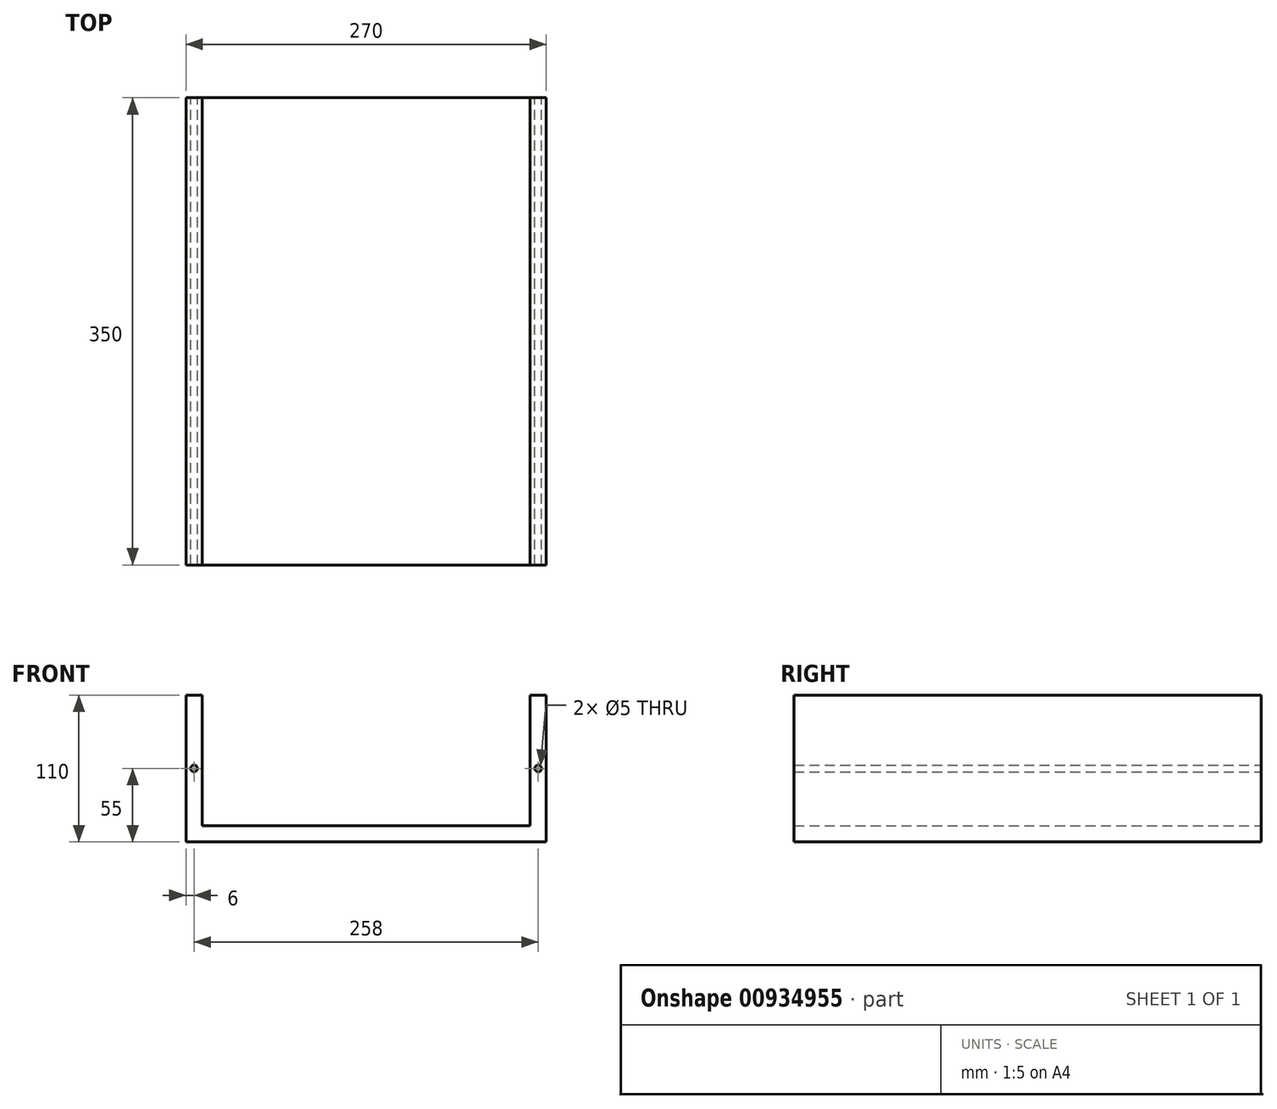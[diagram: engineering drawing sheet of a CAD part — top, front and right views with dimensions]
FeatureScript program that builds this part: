
annotation { "Feature Type Name" : "Feature", "Feature Type Description" : "" }
export const myFeature = defineFeature(function(context is Context, id is Id, definition is map)
    precondition{}
    {
        {
            var Q0;
            Q0=qCreatedBy(makeId("Front.planeOp"),FACE);
            var sketch = newSketch(context, id + "F0", { "sketchPlane" : qUnion([Q0])});
            skLineSegment(sketch, "E0", {"start": v(0, 0) * mm, "end": v(270, 0) * mm});
            skLineSegment(sketch, "E1", {"start": v(0, 0) * mm, "end": v(0, 110) * mm});
            skLineSegment(sketch, "E2.MirrorCS", {"start": v(270, 0) * mm, "end": v(270, 110) * mm});
            skPoint(sketch, "E3.start.orphan", {"position": v(135, 0) * mm});
            skLineSegment(sketch, "E4", {"start": v(0, 110) * mm, "end": v(12, 110) * mm});
            skLineSegment(sketch, "E5", {"start": v(12, 110) * mm, "end": v(12, 12) * mm});
            skLineSegment(sketch, "E6.MirrorCS", {"start": v(270, 110) * mm, "end": v(258, 110) * mm});
            skLineSegment(sketch, "E7.MirrorCS", {"start": v(258, 110) * mm, "end": v(258, 12) * mm});
            skLineSegment(sketch, "E8", {"start": v(12, 12) * mm, "end": v(258, 12) * mm});
            skCircle(sketch, "E9", {"center": v(264, 55) * mm, "radius": 2.5 * mm});
            skPoint(sketch, "E10.orphan", {"position": v(264, 110) * mm});
            skPoint(sketch, "E11.trimOffspring.end.orphan", {"position": v(264, 0) * mm});
            skCircle(sketch, "E12.MirrorC", {"center": v(6, 55) * mm, "radius": 2.5 * mm});
            skLineSegment(sketch, "E13", {"start": v(264, 55) * mm, "end": v(264, 52.5) * mm});
            skSolve(sketch);
        }
        {
            var Q0;
            Q0 = qSketchRegion(id + "F0", true);
            extrude(context, id + "F1", {"entities" : qUnion([Q0]), "depth" : 350 * mm, "offsetDistance" : 25 * mm});
        }
    });
